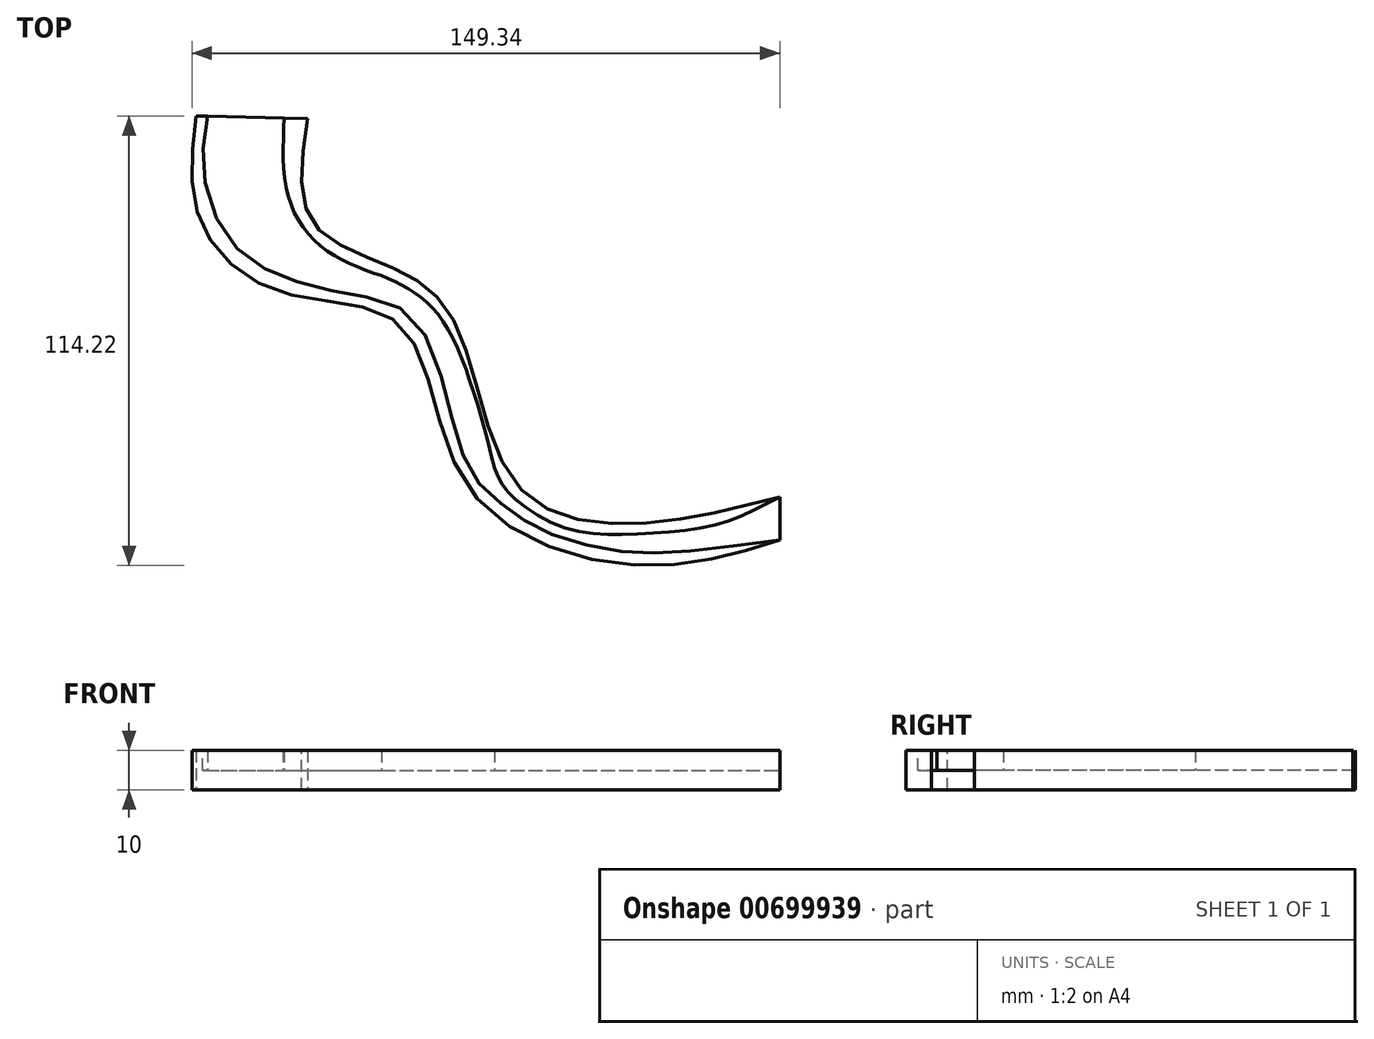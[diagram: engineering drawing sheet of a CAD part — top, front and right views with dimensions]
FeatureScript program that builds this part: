
annotation { "Feature Type Name" : "Feature", "Feature Type Description" : "" }
export const myFeature = defineFeature(function(context is Context, id is Id, definition is map)
    precondition{}
    {
        {
            var Q0;
            Q0=qCreatedBy(makeId("Top.planeOp"),FACE);
            var sketch = newSketch(context, id + "F0", { "sketchPlane" : qUnion([Q0])});
            skFitSpline(sketch, "E0", {"points": [v(-73.14, 65.47) * mm, v(-71.91, 38.61) * mm, v(-51.16, 20.6) * mm, v(-20.94, 12.06) * mm, v(-4.15, -28.54) * mm, v(39.5, -48.68) * mm, v(75.2, -42.27) * mm], "startDerivative": vector(-21.04, -193.23) * mm, "endDerivative": vector(196.5, 61.9) * mm});
            skFitSpline(sketch, "E1", {"points": [v(-44.75, 64.86) * mm, v(-43.53, 38.61) * mm, v(-23.38, 27.01) * mm, v(-6.9, 12.06) * mm, v(8.67, -28.54) * mm, v(39.5, -38) * mm, v(75.2, -31.29) * mm], "startDerivative": vector(-28.51, -193.08) * mm, "endDerivative": vector(192.29, 49.78) * mm});
            skLineSegment(sketch, "E2", {"start": v(-73.14, 65.47) * mm, "end": v(-44.75, 64.86) * mm});
            skLineSegment(sketch, "E3", {"start": v(75.2, -31.29) * mm, "end": v(75.2, -42.27) * mm});
            skSolve(sketch);
        }
        {
            var Q0;
            Q0 = qSketchRegion(id + "F0", true);
            extrude(context, id + "F1", {"entities" : qUnion([Q0]), "depth" : 5 * mm, "offsetDistance" : 25 * mm});
        }
        {
            var Q0;
            Q0=makeQuery(id+"F1.opExtrude","CAP_FACE",FACE,{"disambiguationData":[OSD([sQuery(id+"F0.wireOp",EDGE,"E0"),sQuery(id+"F0.wireOp",EDGE,"E1"),sQuery(id+"F0.wireOp",EDGE,"E2"),sQuery(id+"F0.wireOp",EDGE,"E3")])],"isStart":false});
            var sketch = newSketch(context, id + "F2", { "sketchPlane" : qUnion([Q0])});
            skFitSpline(sketch, "E4", {"points": [v(-70.23, 65.4) * mm, v(-71.17, 50.52) * mm, v(-64.15, 33.42) * mm, v(-51.02, 24.57) * mm, v(-34.24, 20.3) * mm, v(-18.36, 14.5) * mm, v(-8.9, -8.09) * mm, v(-2.8, -25.8) * mm, v(6.1, -34.31) * mm, v(16.43, -40.44) * mm, v(33.53, -45.02) * mm, v(48.79, -45.33) * mm, v(75.2, -42.27) * mm], "startDerivative": vector(-30.71, -185.82) * mm, "endDerivative": vector(275.92, 36.34) * mm});
            skFitSpline(sketch, "E5", {"points": [v(-50.72, 65) * mm, v(-49.5, 44.41) * mm, v(-40.34, 31.6) * mm, v(-26, 24.88) * mm], "startDerivative": vector(-2.7, -59.85) * mm, "endDerivative": vector(47.75, -16.96) * mm});
            skFitSpline(sketch, "E6", {"points": [v(-26, 24.88) * mm, v(-11.65, 15.1) * mm, v(2.75, -23.98) * mm], "startDerivative": vector(39.1, -17.16) * mm, "endDerivative": vector(19.67, -76.27) * mm});
            skFitSpline(sketch, "E7", {"points": [v(2.75, -23.98) * mm, v(6.1, -30.04) * mm, v(19.83, -38.89) * mm, v(38.14, -40.73) * mm, v(59.2, -38.28) * mm, v(75.2, -31.29) * mm], "startDerivative": vector(20.63, -54.42) * mm, "endDerivative": vector(78.56, 41.4) * mm});
            skSolve(sketch);
        }
        {
            var Q0;
            {var subQ0=sQuery(id+"F2.wireOp",EDGE,"E4");Q0=makeQuery(id+"F2.imprint","IMPRINT",FACE,{"disambiguationData":[TD([[makeQuery(id+"F2.imprint","IMPRINT",EDGE,{"derivedFrom":subQ0}),-1.0]])]});}
            var Q1;
            {var subQ1=sQuery(id+"F2.wireOp",EDGE,"E5");Q1=makeQuery(id+"F2.imprint","IMPRINT",FACE,{"disambiguationData":[TD([[makeQuery(id+"F2.imprint","IMPRINT",EDGE,{"derivedFrom":subQ1}),1.0]])]});}
            extrude(context, id + "F3", {"entities" : qUnion([Q0, Q1]), "operationType" : NewBodyOperationType.ADD, "depth" : 5 * mm, "offsetDistance" : 25 * mm});
        }
    });
